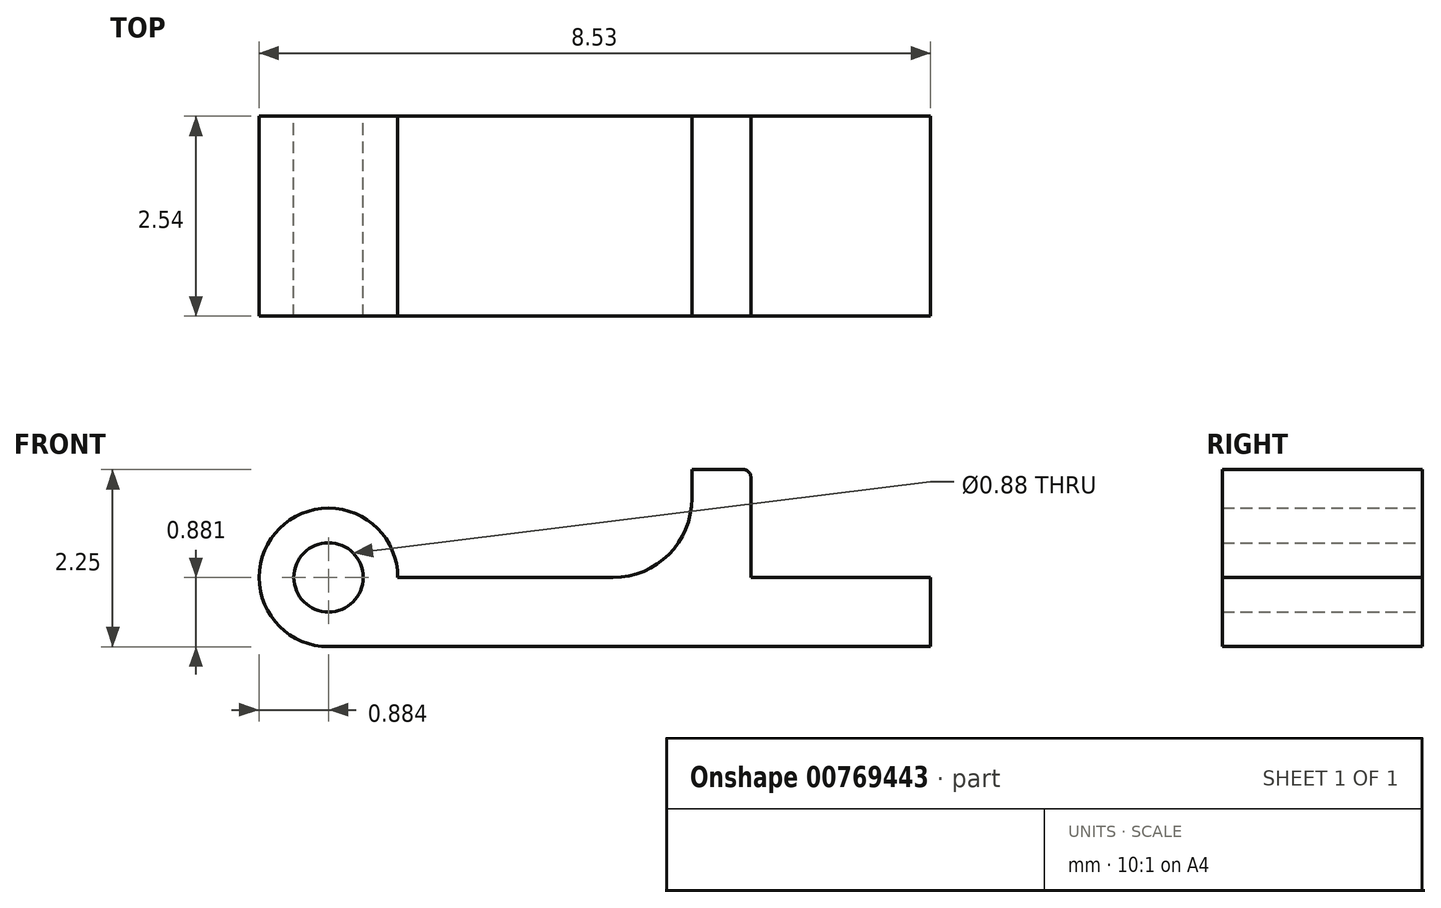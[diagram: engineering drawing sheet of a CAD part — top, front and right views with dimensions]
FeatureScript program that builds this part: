
annotation { "Feature Type Name" : "Feature", "Feature Type Description" : "" }
export const myFeature = defineFeature(function(context is Context, id is Id, definition is map)
    precondition{}
    {
        {
            var Q0;
            Q0=qCreatedBy(makeId("Front.planeOp"),FACE);
            var sketch = newSketch(context, id + "F0", { "sketchPlane" : qUnion([Q0])});
            skLineSegment(sketch, "E0.bottom", {"start": v(36.56, -10.09) * mm, "end": v(39.3, -10.09) * mm});
            skLineSegment(sketch, "E0.top", {"start": v(35.68, -10.97) * mm, "end": v(43.33, -10.97) * mm});
            skLineSegment(sketch, "E0.right", {"start": v(43.33, -10.09) * mm, "end": v(43.33, -10.97) * mm});
            skPoint(sketch, "E1.center.orphan", {"position": v(35.68, -10.53) * mm});
            skCircle(sketch, "E2", {"center": v(35.68, -10.09) * mm, "radius": 0.44 * mm});
            skArc(sketch, "E3", {"start": v(36.56, -10.09) * mm, "mid": v(35.06, -9.47) * mm, "end": v(35.68, -10.97) * mm});
            skLineSegment(sketch, "E4", {"start": v(43.33, -10.97) * mm, "end": v(40.3, -10.97) * mm});
            skLineSegment(sketch, "E5", {"start": v(40.3, -9.09) * mm, "end": v(40.3, -8.72) * mm});
            skLineSegment(sketch, "E6", {"start": v(40.3, -8.72) * mm, "end": v(40.95, -8.72) * mm});
            skLineSegment(sketch, "E7", {"start": v(41.05, -8.82) * mm, "end": v(41.05, -10.09) * mm});
            skLineSegment(sketch, "E8", {"start": v(41.05, -8.82) * mm, "end": v(41.05, -8.92) * mm});
            skArc(sketch, "E9", {"start": v(41.05, -8.82) * mm, "mid": v(41.02, -8.75) * mm, "end": v(40.95, -8.72) * mm});
            skPoint(sketch, "E10.orphan", {"position": v(41.05, -8.72) * mm});
            skLineSegment(sketch, "E11", {"start": v(39.3, -10.09) * mm, "end": v(38.3, -10.09) * mm});
            skArc(sketch, "E12", {"start": v(39.3, -10.09) * mm, "mid": v(40, -9.8) * mm, "end": v(40.3, -9.09) * mm});
            skPoint(sketch, "E13.start.orphan", {"position": v(38.3, -8.09) * mm});
            skPoint(sketch, "E14.start.orphan", {"position": v(40.3, -8.09) * mm});
            skLineSegment(sketch, "E15.trimOffspring", {"start": v(41.05, -10.09) * mm, "end": v(43.33, -10.09) * mm});
            skPoint(sketch, "E16.end.orphan", {"position": v(40.3, -10.09) * mm});
            skPoint(sketch, "E17.orphan", {"position": v(40.3, -8.92) * mm});
            skPoint(sketch, "E18.orphan", {"position": v(40.85, -8.92) * mm});
            skPoint(sketch, "E19.start.orphan", {"position": v(40.85, -8.72) * mm});
            skPoint(sketch, "E20.orphan", {"position": v(36.12, -10.09) * mm});
            skSolve(sketch);
        }
        {
            var Q0;
            Q0=makeQuery(id+"F0.imprint","IMPRINT",FACE,{"disambiguationData":[TD([[makeQuery(id+"F0.imprint","IMPRINT",EDGE,{"derivedFrom":sQuery(id+"F0.wireOp",EDGE,"E0.bottom")}),-1.0]])]});
            extrude(context, id + "F1", {"entities" : qUnion([Q0]), "depth" : 2.54 * mm, "offsetDistance" : 25.4 * mm});
        }
    });
